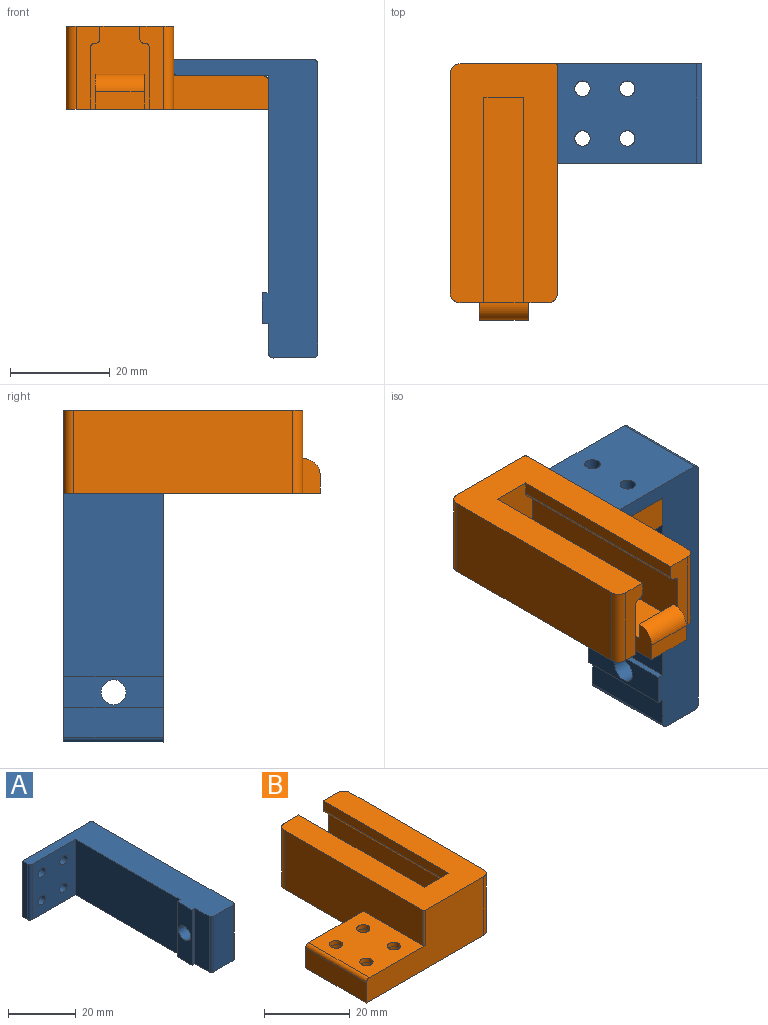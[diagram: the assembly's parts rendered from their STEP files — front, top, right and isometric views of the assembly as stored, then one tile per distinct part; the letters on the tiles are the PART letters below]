
ASSEMBLY  parts=2 mates=1
PART A: 21 faces, bbox 29x60x20 mm
  f0: plane 43.6x20mm, normal (-1,0,0), area 872mm2, adj f2,f3,f8,f10
  f1: plane 20x2.3mm, normal (-1,0,0), area 46mm2, adj f2,f3,f4,f19
  f2: plane 60x29mm, normal (0,0,1), area 669.3mm2, adj f0,f1,f4,f5,f6,f7,f8,f10
  f3: plane 60x29mm, normal (0,0,-1), area 669.3mm2, adj f0,f1,f4,f5,f6,f7,f8,f10
  f4: plane 28x20mm, normal (0,1,0), area 529.8mm2, adj f1,f2,f3,f15,f16,f17,f18,f20
  f5: plane 20x8mm, normal (0,-1,0), area 160mm2, adj f2,f3,f13,f14
  f6: plane 58x20mm, normal (1,0,0), area 1140.4mm2, adj f2,f3,f9,f14,f20
  f7: plane 20x5.9mm, normal (-1,0,0), area 118mm2, adj f2,f3,f11,f13
  f8: plane 20x18mm, normal (0,-1,0), area 329.8mm2, adj f0,f2,f3,f15,f16,f17,f18,f19
  f9: cylinder r=2.5mm len=11.2mm, axis (1,0,0), area 175.9mm2, adj f6,f12
  f10: plane 20x1.2mm, normal (0,1,0), area 24mm2, adj f0,f2,f3,f12
  f11: plane 20x1.2mm, normal (0,-1,0), area 24mm2, adj f2,f3,f7,f12
  f12: plane 20x6.2mm, normal (-1,0,0), area 104.4mm2, adj f2,f3,f9,f10,f11
  f13: cylinder r=1mm len=20mm, axis (0,0,-1), area 31.4mm2, adj f2,f3,f5,f7
  f14: cylinder r=1mm len=20mm, axis (0,0,1), area 31.4mm2, adj f2,f3,f5,f6
  f15: cylinder r=1.55mm len=3.3mm, axis (0,1,0), area 32.1mm2, adj f4,f8
  f16: cylinder r=1.55mm len=3.3mm, axis (0,1,0), area 32.1mm2, adj f4,f8
  f17: cylinder r=1.55mm len=3.3mm, axis (0,1,0), area 32.1mm2, adj f4,f8
  f18: cylinder r=1.55mm len=3.3mm, axis (0,1,0), area 32.1mm2, adj f4,f8
  f19: cylinder r=1mm len=20mm, axis (0,0,-1), area 31.4mm2, adj f1,f2,f3,f8
  f20: cylinder r=1mm len=20mm, axis (0,0,-1), area 31.4mm2, adj f2,f3,f4,f6
PART B: 44 faces, bbox 40.6x51.5x16.7 mm
  f0: plane 41.2x9.8mm, normal (0,0,1), area 403.8mm2, adj f8,f14,f15,f18
  f1: plane 48x21.6mm, normal (0,0,1), area 704.6mm2, adj f2,f3,f5,f6,f11,f15,f16,f17
  f2: plane 44x16.7mm, normal (1,0,0), area 734.8mm2, adj f1,f7,f40,f41
  f3: plane 41.2x2.5mm, normal (-1,0,0), area 103mm2, adj f1,f15,f16,f21
  f4: plane 9.8x3.5mm, normal (0,1,0), area 34.3mm2, adj f7,f8,f14,f19
  f5: plane 45.5x16.7mm, normal (-1,0,0), area 629.2mm2, adj f1,f7,f24,f25,f39,f42
  f6: plane 38.6x16.7mm, normal (0,-1,0), area 449.4mm2, adj f1,f7,f24,f26,f41,f42,f43
  f7: plane 51.5x40.6mm, normal (0,0,-1), area 1271.1mm2, adj f2,f4,f5,f6,f8,f9,f13,f14
  f8: plane 44.7x7mm, normal (1,0,0), area 166.1mm2, adj f0,f4,f7,f15,f18,f19
  f9: plane 41.2x12.4mm, normal (-1,0,0), area 510.9mm2, adj f7,f15,f16,f22
  f10: plane 41.2x0.1mm, normal (0,0,-1), area 4.1mm2, adj f15,f16,f21,f22
  f11: plane 41.2x2.5mm, normal (1,0,0), area 103mm2, adj f1,f15,f17,f20
  f12: plane 41.2x0.1mm, normal (0,0,-1), area 4.1mm2, adj f15,f17,f20,f23
  f13: plane 41.2x12.4mm, normal (1,0,0), area 510.9mm2, adj f7,f15,f17,f23
  f14: plane 44.7x7mm, normal (-1,0,0), area 166.1mm2, adj f0,f4,f7,f15,f18,f19
  f15: plane 16.7x11.8mm, normal (0,1,0), area 149.6mm2, adj f0,f1,f3,f7,f8,f9,f10,f11
  f16: plane 16.7x4.8mm, normal (0,1,0), area 55mm2, adj f1,f3,f7,f9,f10,f21,f22,f40
  f17: plane 16.7x4.8mm, normal (0,1,0), area 55mm2, adj f1,f7,f11,f12,f13,f20,f23,f39
  f18: plane 9.8x3.5mm, normal (0,-1,0), area 34.3mm2, adj f0,f8,f14,f19
  f19: cylinder r=3.5mm len=9.8mm, axis (1,0,0), area 53.9mm2, adj f4,f8,f14,f18
  f20: cylinder r=1mm len=41.2mm, axis (0,-1,0), area 64.7mm2, adj f11,f12,f15,f17
  f21: cylinder r=1mm len=41.2mm, axis (0,1,0), area 64.7mm2, adj f3,f10,f15,f16
  f22: cylinder r=0.8mm len=41.2mm, axis (0,1,0), area 51.8mm2, adj f9,f10,f15,f16
  f23: cylinder r=0.8mm len=41.2mm, axis (0,-1,0), area 51.8mm2, adj f12,f13,f15,f17
  f24: plane 20x18.5mm, normal (0,0,1), area 329.9mm2, adj f5,f6,f25,f35,f36,f37,f38,f42
  f25: plane 19x6.7mm, normal (0,1,0), area 127.1mm2, adj f5,f7,f24,f26,f43
  f26: plane 20x5.7mm, normal (-1,0,0), area 114mm2, adj f6,f7,f25,f43
  f27: cylinder r=2.75mm len=5.5mm, axis (0,0,-1), area 95mm2, adj f7,f28
  f28: plane 5.5x5.5mm, normal (0,0,-1), area 16.2mm2, adj f27,f38
  f29: cylinder r=2.75mm len=5.5mm, axis (0,0,-1), area 95mm2, adj f7,f30
  f30: plane 5.5x5.5mm, normal (0,0,-1), area 16.2mm2, adj f29,f37
  f31: cylinder r=2.75mm len=5.5mm, axis (0,0,-1), area 95mm2, adj f7,f32
  f32: plane 5.5x5.5mm, normal (0,0,-1), area 16.2mm2, adj f31,f36
  f33: cylinder r=2.75mm len=5.5mm, axis (0,0,-1), area 95mm2, adj f7,f34
  f34: plane 5.5x5.5mm, normal (0,0,-1), area 16.2mm2, adj f33,f35
  f35: cylinder r=1.55mm len=3.1mm, axis (0,0,-1), area 11.7mm2, adj f24,f34
  f36: cylinder r=1.55mm len=3.1mm, axis (0,0,-1), area 11.7mm2, adj f24,f32
  f37: cylinder r=1.55mm len=3.1mm, axis (0,0,-1), area 11.7mm2, adj f24,f30
  f38: cylinder r=1.55mm len=3.1mm, axis (0,0,-1), area 11.7mm2, adj f24,f28
  f39: cylinder r=2mm len=16.7mm, axis (0,0,-1), area 52.5mm2, adj f1,f5,f7,f17
  f40: cylinder r=2mm len=16.7mm, axis (0,0,-1), area 52.5mm2, adj f1,f2,f7,f16
  f41: cylinder r=2mm len=16.7mm, axis (0,0,1), area 52.5mm2, adj f1,f2,f6,f7
  f42: cylinder r=0.5mm len=10mm, axis (0,0,-1), area 7.9mm2, adj f1,f5,f6,f24
  f43: cylinder r=1mm len=20mm, axis (0,-1,0), area 31.4mm2, adj f6,f24,f25,f26
PLACE A rot(axis=(1,0,0),90deg) t=(9.94,-5.3,9.72)mm
PLACE B rot(axis=(0,0,-1),180deg) t=(9.94,-56.8,-0.28)mm
MATE fastened B.f29 <-> A.f17  axis (0,0,1) through (14.94,-10.3,6.42)mm
